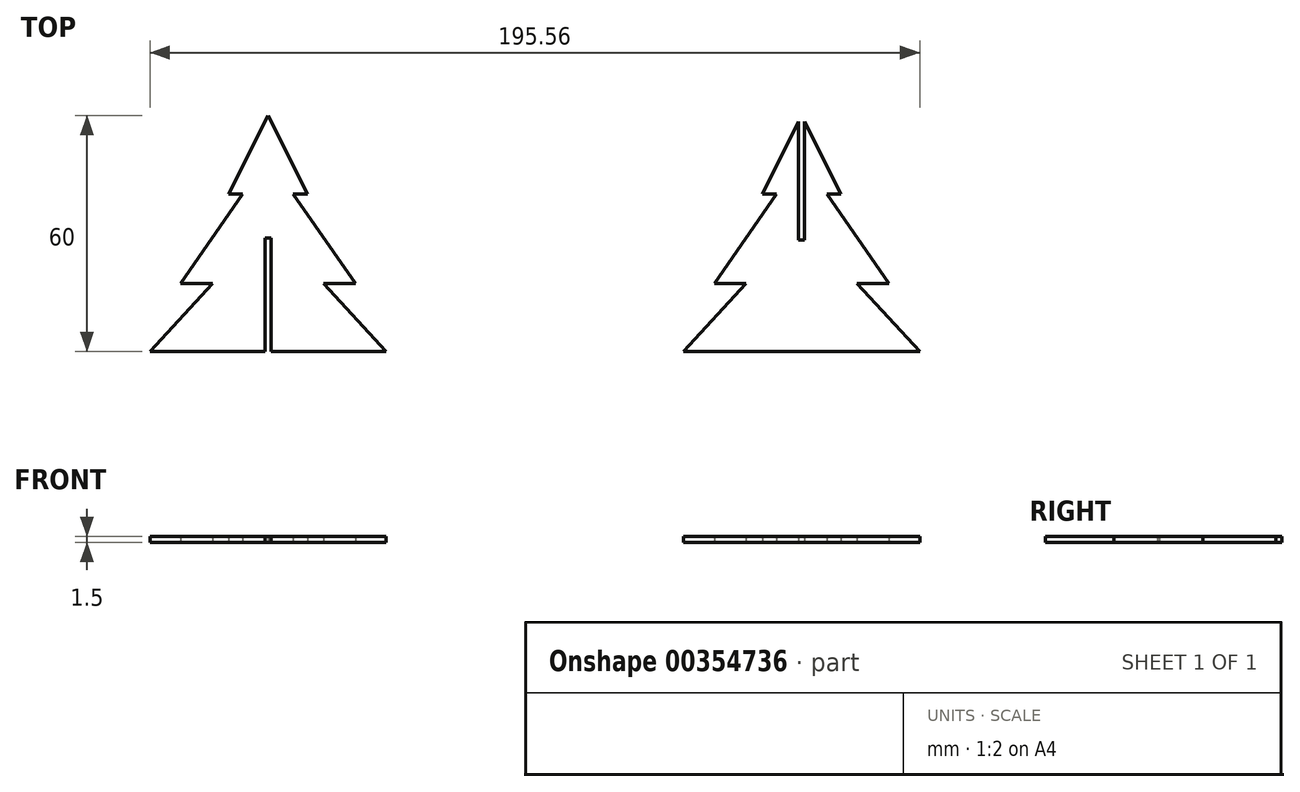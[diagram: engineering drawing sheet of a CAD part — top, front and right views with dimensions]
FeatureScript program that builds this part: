
annotation { "Feature Type Name" : "Feature", "Feature Type Description" : "" }
export const myFeature = defineFeature(function(context is Context, id is Id, definition is map)
    precondition{}
    {
        {
            var Q0;
            Q0=qCreatedBy(makeId("Top.planeOp"),FACE);
            var sketch = newSketch(context, id + "F0", { "sketchPlane" : qUnion([Q0])});
            skLineSegment(sketch, "E0", {"start": v(0, 0) * mm, "end": v(30, 0) * mm});
            skLineSegment(sketch, "E1", {"start": v(0, 0) * mm, "end": v(0, 17.3) * mm, "construction": true});
            skLineSegment(sketch, "E2", {"start": v(0, 17.3) * mm, "end": v(0, 40) * mm, "construction": true});
            skLineSegment(sketch, "E3", {"start": v(0, 40) * mm, "end": v(0, 60) * mm, "construction": true});
            skLineSegment(sketch, "E4", {"start": v(30, 0) * mm, "end": v(14.07, 17.3) * mm});
            skLineSegment(sketch, "E5", {"start": v(14.07, 17.3) * mm, "end": v(22.18, 17.3) * mm});
            skLineSegment(sketch, "E6", {"start": v(22.18, 17.3) * mm, "end": v(6.4, 40) * mm});
            skLineSegment(sketch, "E7", {"start": v(6.4, 40) * mm, "end": v(10, 40) * mm});
            skLineSegment(sketch, "E8.MirrorCS", {"start": v(-6.4, 40) * mm, "end": v(-10, 40) * mm});
            skLineSegment(sketch, "E9.MirrorCS", {"start": v(-14.07, 17.3) * mm, "end": v(-22.18, 17.3) * mm});
            skLineSegment(sketch, "E10.MirrorCS", {"start": v(-30, 0) * mm, "end": v(-14.07, 17.3) * mm});
            skLineSegment(sketch, "E11.MirrorCS", {"start": v(0, 0) * mm, "end": v(-30, 0) * mm});
            skLineSegment(sketch, "E12", {"start": v(-0.75, 28.65) * mm, "end": v(-0.75, 58.5) * mm});
            skLineSegment(sketch, "E13.MirrorCS", {"start": v(0.75, 28.65) * mm, "end": v(0.75, 58.5) * mm});
            skLineSegment(sketch, "E14", {"start": v(0.75, 58.5) * mm, "end": v(10, 40) * mm});
            skLineSegment(sketch, "E15", {"start": v(-0.75, 58.5) * mm, "end": v(-10, 40) * mm});
            skLineSegment(sketch, "E16", {"start": v(-6.4, 40) * mm, "end": v(-22.18, 17.3) * mm});
            skLineSegment(sketch, "E17", {"start": v(-67.78, 64.41) * mm, "end": v(-67.78, -1.9) * mm, "construction": true});
            skLineSegment(sketch, "E18.MirrorCS", {"start": v(-134.8, 58.5) * mm, "end": v(-125.56, 40) * mm});
            skLineSegment(sketch, "E19.MirrorCS", {"start": v(-136.3, 58.5) * mm, "end": v(-145.56, 40) * mm});
            skLineSegment(sketch, "E20.MirrorCS", {"start": v(-129.16, 40) * mm, "end": v(-113.38, 17.3) * mm});
            skLineSegment(sketch, "E21.MirrorCS", {"start": v(-149.63, 17.3) * mm, "end": v(-157.74, 17.3) * mm});
            skLineSegment(sketch, "E22.MirrorCS", {"start": v(-165.56, 0) * mm, "end": v(-149.63, 17.3) * mm});
            skLineSegment(sketch, "E23.MirrorCS", {"start": v(-105.56, 0) * mm, "end": v(-121.49, 17.3) * mm});
            skLineSegment(sketch, "E24.MirrorCS", {"start": v(-121.49, 17.3) * mm, "end": v(-113.38, 17.3) * mm});
            skLineSegment(sketch, "E25.MirrorCS", {"start": v(-141.96, 40) * mm, "end": v(-145.56, 40) * mm});
            skLineSegment(sketch, "E26.MirrorCS", {"start": v(-129.16, 40) * mm, "end": v(-125.56, 40) * mm});
            skLineSegment(sketch, "E27.MirrorCS", {"start": v(-157.74, 17.3) * mm, "end": v(-141.96, 40) * mm});
            skLineSegment(sketch, "E28", {"start": v(-145.56, 40) * mm, "end": v(-135.56, 60) * mm});
            skLineSegment(sketch, "E29", {"start": v(-125.56, 40) * mm, "end": v(-135.56, 60) * mm});
            skLineSegment(sketch, "E30", {"start": v(-136.3, 0) * mm, "end": v(-165.56, 0) * mm});
            skLineSegment(sketch, "E31", {"start": v(-134.8, 0) * mm, "end": v(-105.56, 0) * mm});
            skLineSegment(sketch, "E32", {"start": v(-136.3, 28.65) * mm, "end": v(-136.3, 0) * mm});
            skLineSegment(sketch, "E33", {"start": v(-134.8, 28.65) * mm, "end": v(-134.8, 0) * mm});
            skLineSegment(sketch, "E34", {"start": v(-0.75, 58.5) * mm, "end": v(-0.75, 28.65) * mm});
            skLineSegment(sketch, "E35", {"start": v(-0.75, 28.65) * mm, "end": v(-0.75, 28.4) * mm});
            skLineSegment(sketch, "E36", {"start": v(0.75, 28.65) * mm, "end": v(0.75, 28.4) * mm});
            skLineSegment(sketch, "E37", {"start": v(-0.75, 28.4) * mm, "end": v(0.75, 28.4) * mm});
            skLineSegment(sketch, "E38", {"start": v(-136.3, 28.65) * mm, "end": v(-136.3, 28.9) * mm});
            skLineSegment(sketch, "E39", {"start": v(-134.8, 28.65) * mm, "end": v(-134.8, 28.9) * mm});
            skLineSegment(sketch, "E40", {"start": v(-136.3, 28.9) * mm, "end": v(-134.8, 28.9) * mm});
            skSolve(sketch);
        }
        {
            var Q0;
            Q0=makeQuery(id+"F0.imprint","IMPRINT",FACE,{"disambiguationData":[TD([[makeQuery(id+"F0.imprint","IMPRINT",EDGE,{"derivedFrom":sQuery(id+"F0.wireOp",EDGE,"E21.MirrorCS")}),-1.0]])]});
            var Q1;
            Q1=makeQuery(id+"F0.imprint","IMPRINT",FACE,{"disambiguationData":[TD([[makeQuery(id+"F0.imprint","IMPRINT",EDGE,{"derivedFrom":sQuery(id+"F0.wireOp",EDGE,"E0")}),1.0]])]});
            extrude(context, id + "F1", {"entities" : qUnion([Q0, Q1]), "depth" : 1.5 * mm});
        }
    });
